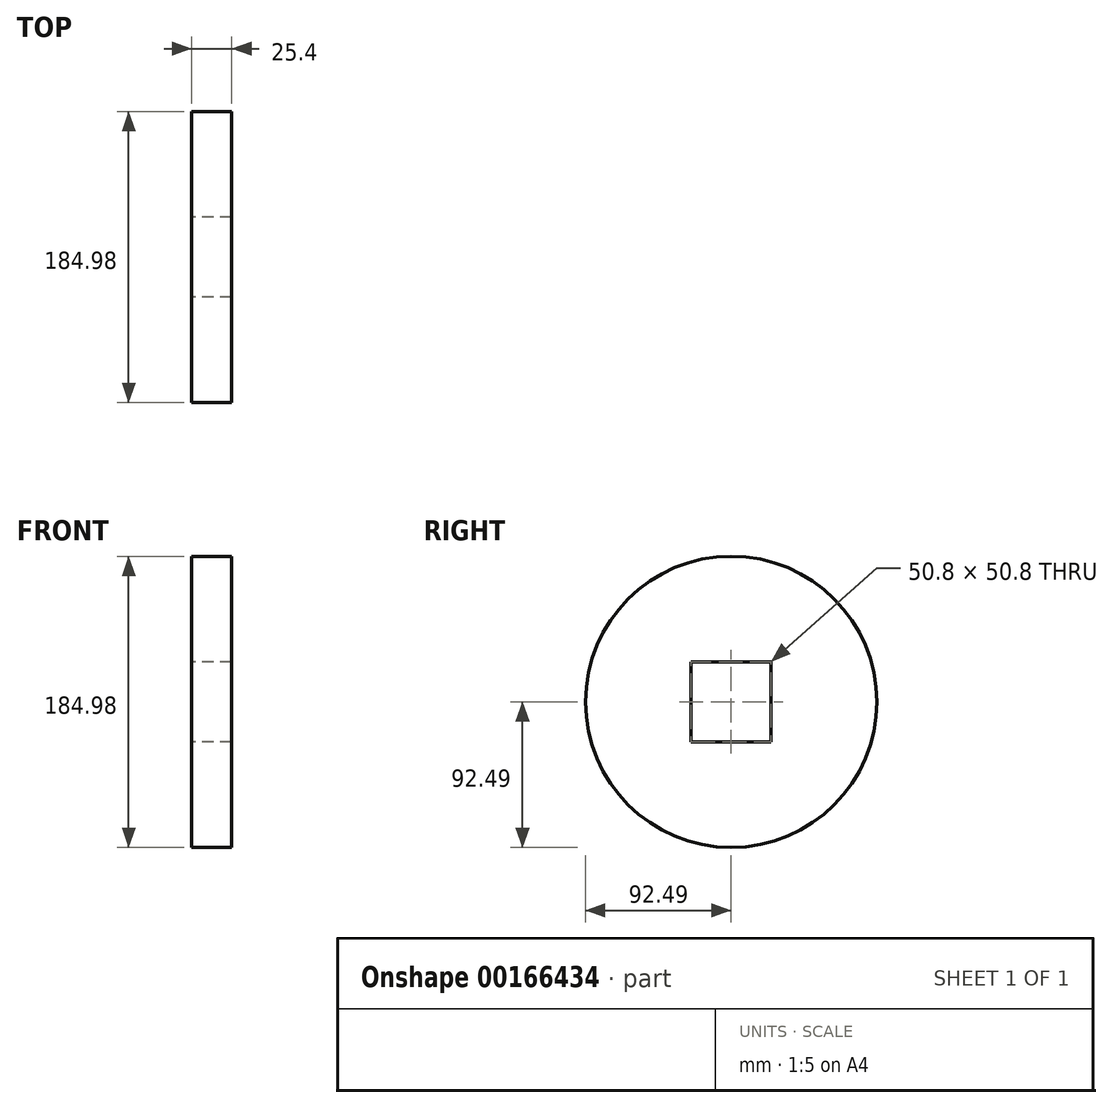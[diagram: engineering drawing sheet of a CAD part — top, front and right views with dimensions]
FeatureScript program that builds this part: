
annotation { "Feature Type Name" : "Feature", "Feature Type Description" : "" }
export const myFeature = defineFeature(function(context is Context, id is Id, definition is map)
    precondition{}
    {
        {
            var Q0;
            Q0=qCreatedBy(makeId("Right.planeOp"),FACE);
            var sketch = newSketch(context, id + "F0", { "sketchPlane" : qUnion([Q0])});
            skCircle(sketch, "E0", {"center": v(0, 0) * mm, "radius": 92.49 * mm});
            skLineSegment(sketch, "E1.bottom", {"start": v(25.4, 25.4) * mm, "end": v(-25.4, 25.4) * mm});
            skLineSegment(sketch, "E1.top", {"start": v(25.4, -25.4) * mm, "end": v(-25.4, -25.4) * mm});
            skLineSegment(sketch, "E1.left", {"start": v(25.4, 25.4) * mm, "end": v(25.4, -25.4) * mm});
            skLineSegment(sketch, "E1.right", {"start": v(-25.4, 25.4) * mm, "end": v(-25.4, -25.4) * mm});
            skSolve(sketch);
        }
        {
            var Q0;
            Q0=makeQuery(id+"F0.imprint","IMPRINT",FACE,{"disambiguationData":[TD([[makeQuery(id+"F0.imprint","IMPRINT",EDGE,{"derivedFrom":sQuery(id+"F0.wireOp",EDGE,"E0")}),1.0]])]});
            extrude(context, id + "F1", {"entities" : qUnion([Q0]), "endBound" : BoundingType.SYMMETRIC, "depth" : 25.4 * mm});
        }
    });
